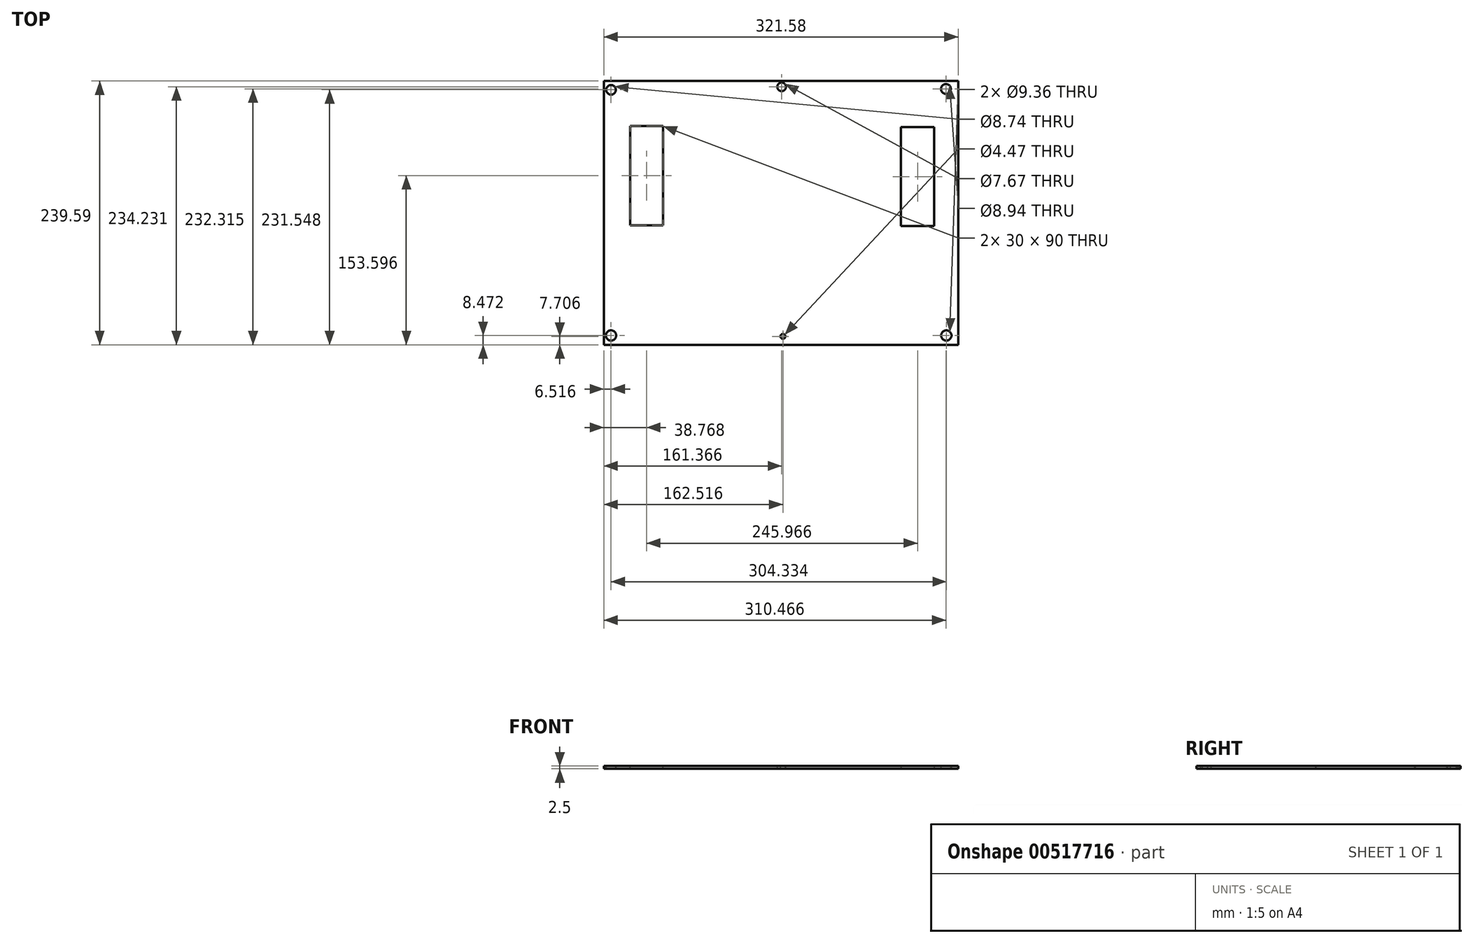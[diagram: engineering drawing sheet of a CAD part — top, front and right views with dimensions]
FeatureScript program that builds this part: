
annotation { "Feature Type Name" : "Feature", "Feature Type Description" : "" }
export const myFeature = defineFeature(function(context is Context, id is Id, definition is map)
    precondition{}
    {
        {
            var Q0;
            Q0=qCreatedBy(makeId("Top.planeOp"),FACE);
            var sketch = newSketch(context, id + "F0", { "sketchPlane" : qUnion([Q0])});
            skLineSegment(sketch, "E0.bottom", {"start": v(-170.02, 70.74) * mm, "end": v(151.56, 70.74) * mm});
            skLineSegment(sketch, "E0.top", {"start": v(-170.02, -168.85) * mm, "end": v(151.56, -168.85) * mm});
            skLineSegment(sketch, "E0.left", {"start": v(-170.02, 70.74) * mm, "end": v(-170.02, -168.85) * mm});
            skLineSegment(sketch, "E0.right", {"start": v(151.56, 70.74) * mm, "end": v(151.56, -168.85) * mm});
            skSolve(sketch);
        }
        {
            var Q0;
            Q0 = qSketchRegion(id + "F0", true);
            extrude(context, id + "F1", {"entities" : qUnion([Q0]), "depth" : 2.5 * mm, "offsetDistance" : 25 * mm});
        }
        {
            var Q0;
            Q0=makeQuery(id+"F1.opExtrude","CAP_FACE",FACE,{"disambiguationData":[OSD([sQuery(id+"F0.wireOp",EDGE,"E0.bottom"),sQuery(id+"F0.wireOp",EDGE,"E0.top"),sQuery(id+"F0.wireOp",EDGE,"E0.left"),sQuery(id+"F0.wireOp",EDGE,"E0.right")])],"isStart":false});
            var sketch = newSketch(context, id + "F2", { "sketchPlane" : qUnion([Q0])});
            skLineSegment(sketch, "E1.bottom", {"start": v(-116.25, -60.25) * mm, "end": v(-146.25, -60.25) * mm});
            skLineSegment(sketch, "E1.top", {"start": v(-116.25, 29.75) * mm, "end": v(-146.25, 29.75) * mm});
            skLineSegment(sketch, "E1.left", {"start": v(-116.25, -60.25) * mm, "end": v(-116.25, 29.75) * mm});
            skLineSegment(sketch, "E1.right", {"start": v(-146.25, -60.25) * mm, "end": v(-146.25, 29.75) * mm});
            skSolve(sketch);
        }
        {
            var Q0;
            Q0 = qSketchRegion(id + "F2", true);
            extrude(context, id + "F3", {"entities" : qUnion([Q0]), "operationType" : NewBodyOperationType.REMOVE, "oppositeDirection" : true, "depth" : 30 * mm, "offsetDistance" : 25 * mm});
        }
        {
            var Q0;
            Q0=qCreatedBy(makeId("Top.planeOp"),FACE);
            var sketch = newSketch(context, id + "F4", { "sketchPlane" : qUnion([Q0])});
            skLineSegment(sketch, "E2.bottom", {"start": v(129.71, -61.1) * mm, "end": v(99.71, -61.1) * mm});
            skLineSegment(sketch, "E2.top", {"start": v(129.71, 28.9) * mm, "end": v(99.71, 28.9) * mm});
            skLineSegment(sketch, "E2.left", {"start": v(129.71, -61.1) * mm, "end": v(129.71, 28.9) * mm});
            skLineSegment(sketch, "E2.right", {"start": v(99.71, -61.1) * mm, "end": v(99.71, 28.9) * mm});
            skSolve(sketch);
        }
        {
            var Q0;
            Q0 = qSketchRegion(id + "F4", true);
            extrude(context, id + "F5", {"entities" : qUnion([Q0]), "operationType" : NewBodyOperationType.REMOVE, "oppositeDirection" : true, "depth" : -30 * mm, "offsetDistance" : 25 * mm});
        }
        {
            var Q0;
            Q0=makeQuery(id+"F2.imprint","IMPRINT",FACE,{"disambiguationData":[TD([[makeQuery(id+"F2.imprint","IMPRINT",EDGE,{"derivedFrom":sQuery(id+"F2.wireOp",EDGE,"E1.bottom")}),1.0]])]});
            var sketch = newSketch(context, id + "F6", { "sketchPlane" : qUnion([Q0])});
            skCircle(sketch, "E3", {"center": v(-163.5, 62.7) * mm, "radius": 4.37 * mm});
            skCircle(sketch, "E4", {"center": v(140.45, 63.46) * mm, "radius": 4.47 * mm});
            skCircle(sketch, "E5", {"center": v(-8.65, 65.38) * mm, "radius": 3.83 * mm});
            skCircle(sketch, "E6", {"center": v(-7.5, -161.14) * mm, "radius": 2.23 * mm});
            skCircle(sketch, "E7", {"center": v(-163.5, -160.38) * mm, "radius": 4.68 * mm});
            skCircle(sketch, "E8", {"center": v(140.83, -160.38) * mm, "radius": 4.68 * mm});
            skSolve(sketch);
        }
        {
            var Q0;
            Q0 = qSketchRegion(id + "F6", true);
            extrude(context, id + "F7", {"entities" : qUnion([Q0]), "operationType" : NewBodyOperationType.REMOVE, "oppositeDirection" : true, "depth" : 30 * mm, "offsetDistance" : 25 * mm});
        }
    });
